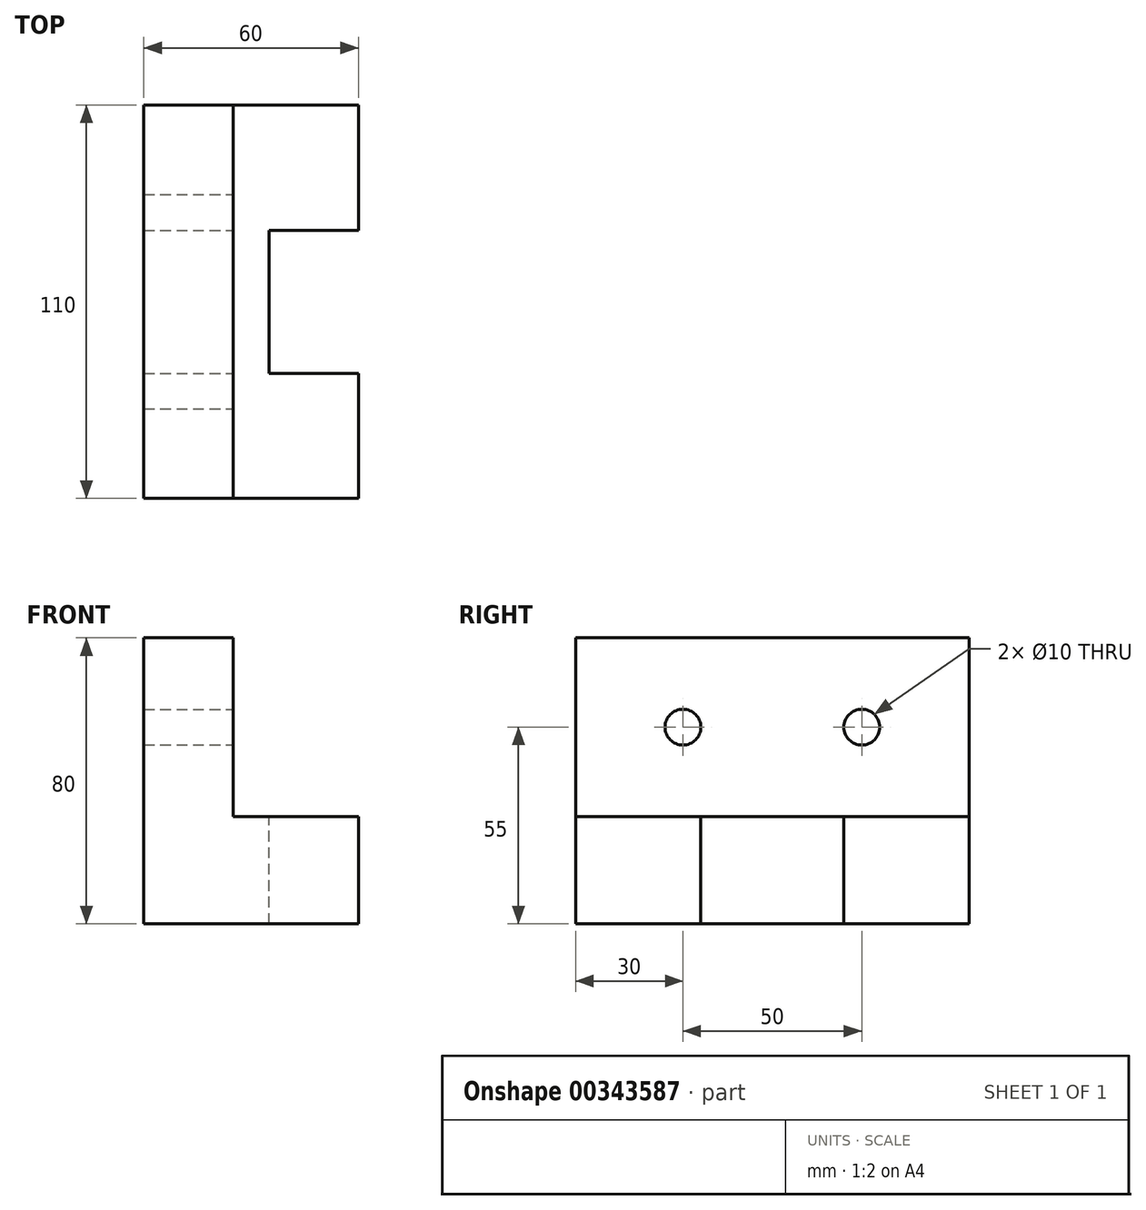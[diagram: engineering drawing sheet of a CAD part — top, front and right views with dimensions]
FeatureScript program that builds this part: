
annotation { "Feature Type Name" : "Feature", "Feature Type Description" : "" }
export const myFeature = defineFeature(function(context is Context, id is Id, definition is map)
    precondition{}
    {
        {
            var Q0;
            Q0=qCreatedBy(makeId("Front.planeOp"),FACE);
            var sketch = newSketch(context, id + "F0", { "sketchPlane" : qUnion([Q0])});
            skLineSegment(sketch, "E0.bottom", {"start": v(0, 0) * mm, "end": v(60, 0) * mm});
            skLineSegment(sketch, "E0.top", {"start": v(0, 80) * mm, "end": v(60, 80) * mm});
            skLineSegment(sketch, "E0.left", {"start": v(0, 0) * mm, "end": v(0, 80) * mm});
            skLineSegment(sketch, "E0.right", {"start": v(60, 0) * mm, "end": v(60, 80) * mm});
            skSolve(sketch);
        }
        {
            var Q0;
            Q0=makeQuery(id+"F0.imprint","IMPRINT",FACE,{"disambiguationData":[TD([[makeQuery(id+"F0.imprint","IMPRINT",EDGE,{"derivedFrom":sQuery(id+"F0.wireOp",EDGE,"E0.bottom")}),1.0]])]});
            extrude(context, id + "F1", {"entities" : qUnion([Q0]), "depth" : 110 * mm});
        }
        {
            var Q0;
            Q0=makeQuery(id+"F1.opExtrude","CAP_FACE",FACE,{"disambiguationData":[OSD([sQuery(id+"F0.wireOp",EDGE,"E0.bottom"),sQuery(id+"F0.wireOp",EDGE,"E0.top"),sQuery(id+"F0.wireOp",EDGE,"E0.left"),sQuery(id+"F0.wireOp",EDGE,"E0.right")])],"isStart":false});
            var sketch = newSketch(context, id + "F2", { "sketchPlane" : qUnion([Q0])});
            skLineSegment(sketch, "E1", {"start": v(25, 80) * mm, "end": v(25, 30) * mm});
            skLineSegment(sketch, "E2", {"start": v(25, 30) * mm, "end": v(60, 30) * mm});
            skSolve(sketch);
        }
        {
            var Q0;
            Q0 = qSketchRegion(id + "F2", true);
            var Q1;
            {var subQ0=sQuery(id+"F2.wireOp",EDGE,"E1");Q1=makeQuery(id+"F2.imprint","IMPRINT",FACE,{"disambiguationData":[TD([[makeQuery(id+"F2.imprint","IMPRINT",EDGE,{"derivedFrom":subQ0}),1.0]])]});}
            extrude(context, id + "F3", {"entities" : qUnion([Q0, Q1]), "operationType" : NewBodyOperationType.REMOVE, "endBound" : BoundingType.THROUGH_ALL, "oppositeDirection" : true, "depth" : 25 * mm});
        }
        {
            var Q0;
            Q0=makeQuery(id+"F3.boolean.opBoolean","COPY",FACE,{"derivedFrom":makeQuery(id+"F3.opExtrude","SWEPT_FACE",FACE,{"disambiguationData":[OSD([sQuery(id+"F2.wireOp",EDGE,"E2")])]})});
            var sketch = newSketch(context, id + "F4", { "sketchPlane" : qUnion([Q0])});
            skLineSegment(sketch, "E3.bottom", {"start": v(60, -75) * mm, "end": v(35, -75) * mm});
            skLineSegment(sketch, "E3.top", {"start": v(60, -35) * mm, "end": v(35, -35) * mm});
            skLineSegment(sketch, "E3.left", {"start": v(60, -75) * mm, "end": v(60, -35) * mm});
            skLineSegment(sketch, "E3.right", {"start": v(35, -75) * mm, "end": v(35, -35) * mm});
            skSolve(sketch);
        }
        {
            var Q0;
            Q0=makeQuery(id+"F4.imprint","IMPRINT",FACE,{"disambiguationData":[TD([[makeQuery(id+"F4.imprint","IMPRINT",EDGE,{"derivedFrom":sQuery(id+"F4.wireOp",EDGE,"E3.bottom")}),-1.0]])]});
            extrude(context, id + "F5", {"entities" : qUnion([Q0]), "operationType" : NewBodyOperationType.REMOVE, "endBound" : BoundingType.THROUGH_ALL, "oppositeDirection" : true, "depth" : 25 * mm});
        }
        {
            var Q0;
            Q0=makeQuery(id+"F3.boolean.opBoolean","COPY",FACE,{"derivedFrom":makeQuery(id+"F3.opExtrude","SWEPT_FACE",FACE,{"disambiguationData":[OSD([sQuery(id+"F2.wireOp",EDGE,"E1")])]})});
            var sketch = newSketch(context, id + "F6", { "sketchPlane" : qUnion([Q0])});
            skPoint(sketch, "E4", {"position": v(-80, 55) * mm});
            skPoint(sketch, "E5", {"position": v(-30, 55) * mm});
            skSolve(sketch);
        }
        {
            var Q0;
            Q0=sQuery(id+"F6.wireOp",VERTEX,"E5");
            var Q1;
            Q1=sQuery(id+"F6.wireOp",VERTEX,"E4");
            var Q2;
            Q2=makeQuery(id+"F1.opExtrude","SWEPT_BODY",BODY,{"disambiguationData":[OSD([sQuery(id+"F0.wireOp",EDGE,"E0.bottom"),sQuery(id+"F0.wireOp",EDGE,"E0.top"),sQuery(id+"F0.wireOp",EDGE,"E0.left"),sQuery(id+"F0.wireOp",EDGE,"E0.right")])]});
            hole(context, id + "F7", {"style" : HoleStyle.SIMPLE, "endStyle" : HoleEndStyle.THROUGH, "holeDiameter" : 10 * mm, "isTappedThrough" : true, "tappedDepth" : 12 * mm, "tapClearance" : 3, "locations" : qUnion([Q0, Q1]), "scope" : qUnion([Q2])});
        }
    });
